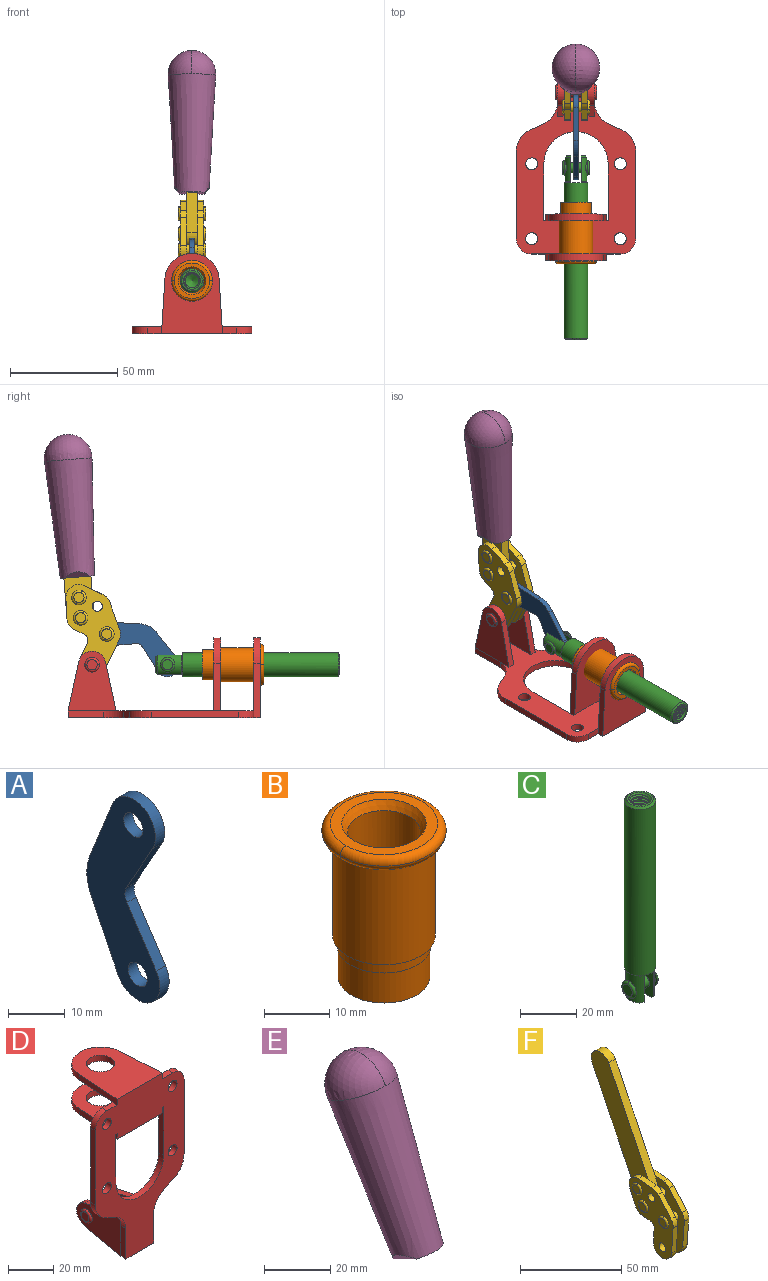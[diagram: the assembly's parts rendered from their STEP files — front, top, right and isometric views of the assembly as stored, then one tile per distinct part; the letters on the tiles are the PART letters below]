
ASSEMBLY  parts=6 mates=6
PART A: 12 faces, bbox 2.3x18.2x42.8 mm
  f0: cylinder r=2.4mm len=4.8mm, axis (1,0,0), area 34.9mm2, adj f4,f11
  f1: cylinder r=10.41mm len=8.47mm, axis (1,0,0), area 20.2mm2, adj f4,f9,f10,f11
  f2: cylinder r=3.05mm len=3.16mm, axis (1,0,0), area 7.7mm2, adj f4,f6,f7,f11
  f3: cylinder r=2.4mm len=4.8mm, axis (1,0,0), area 34.9mm2, adj f4,f11
  f4: plane 42.81x18.23mm, normal (-1,0,0), area 414.1mm2, adj f0,f1,f2,f3,f5,f6,f7,f8
  f5: cylinder r=5.54mm len=10.67mm, axis (1,0,0), area 41.8mm2, adj f4,f6,f10,f11
  f6: plane 11.66x6.53mm, normal (0,-0.87,-0.49), area 30.9mm2, adj f2,f4,f5,f11
  f7: plane 11.17x7.33mm, normal (0,-0.84,0.55), area 30.9mm2, adj f2,f4,f8,f11
  f8: cylinder r=5.54mm len=10.51mm, axis (1,0,0), area 41.8mm2, adj f4,f7,f9,f11
  f9: plane 13.67x6.67mm, normal (0,0.9,-0.44), area 35.1mm2, adj f1,f4,f8,f11
  f10: plane 14.1x5.7mm, normal (0,0.93,0.37), area 35.1mm2, adj f1,f4,f5,f11
  f11: plane 42.81x18.23mm, normal (1,0,0), area 414.1mm2, adj f0,f1,f2,f3,f5,f6,f7,f8
PART B: 15 faces, bbox 20.6x20.6x28.7 mm
  f0: torus R=8.26mm, axis (0,0,1), area 56.8mm2, adj f1,f10,f12
  f1: torus R=8.26mm, axis (0,0,1), area 56.8mm2, adj f0,f6,f13
  f2: cylinder r=5.59mm len=25.91mm, axis (0,0,1), area 909.6mm2, adj f3,f4
  f3: cone r=6.86mm half-angle=45deg, axis (0,0,-1), area 70.2mm2, adj f2,f14
  f4: cone r=6.47mm half-angle=30deg, axis (0,0,1), area 66.7mm2, adj f2,f13
  f5: cylinder r=7.04mm len=14.07mm, axis (0,0,1), area 252.6mm2, adj f11,f14
  f6: torus R=8.26mm, axis (0,0,1), area 56.8mm2, adj f1,f12,f13
  f7: cylinder r=7.16mm len=14.33mm, axis (0,0,1), area 91.5mm2, adj f9,f11
  f8: cylinder r=7.86mm len=18.42mm, axis (0,0,1), area 909.6mm2, adj f9,f10
  f9: plane 15.72x15.72mm, normal (0,0,-1), area 33mm2, adj f7,f8
  f10: plane 16.51x16.51mm, normal (0,0,-1), area 19.9mm2, adj f0,f8,f12
  f11: plane 14.33x14.33mm, normal (0,0,-1), area 5.7mm2, adj f5,f7
  f12: torus R=8.26mm, axis (0,0,1), area 56.8mm2, adj f0,f6,f10
  f13: plane 16.51x16.51mm, normal (0,0,1), area 82.7mm2, adj f1,f4,f6
  f14: plane 14.07x14.07mm, normal (0,0,-1), area 7.8mm2, adj f3,f5
PART C: 48 faces, bbox 12.6x11.1x86.1 mm
  f0: torus R=2.41mm, axis (-1,0,0), area 15mm2, adj f30,f32,f34
  f1: torus R=2.41mm, axis (-1,0,0), area 15mm2, adj f29,f31,f33
  f2: cylinder r=5.54mm len=72.39mm, axis (0,0,1), area 2518.5mm2, adj f3,f4,f42,f43
  f3: cone r=5.54mm half-angle=45deg, axis (0,0,1), area 7.6mm2, adj f2,f5,f41
  f4: cone r=5.54mm half-angle=45deg, axis (0,0,-1), area 34.9mm2, adj f2,f39
  f5: cylinder r=5.08mm len=11.48mm, axis (0,0,1), area 108.3mm2, adj f3,f7,f8,f41
  f6: cylinder r=2.41mm len=4.83mm, axis (-1,0,0), area 71.2mm2, adj f40,f41
  f7: cylinder r=2.41mm len=4.83mm, axis (-1,0,0), area 7.6mm2, adj f5,f34
  f8: cone r=5.08mm half-angle=45deg, axis (0,0,1), area 10.6mm2, adj f5,f37,f41
  f9: cone r=3.98mm half-angle=45deg, axis (0,0,1), area 17.6mm2, adj f27,f39,f45,f46,f47
  f10: cylinder r=2.41mm len=4.83mm, axis (-1,0,0), area 7.6mm2, adj f33,f38
  f11: cylinder r=3.2mm len=6.4mm, axis (0,0,1), area 78.4mm2, adj f12,f28,f44,f45,f47
  f12: cylinder r=3.2mm len=6.4mm, axis (0,0,1), area 10.5mm2, adj f11,f13,f45,f47
  f13: cylinder r=3.2mm len=6.4mm, axis (0,0,1), area 10.5mm2, adj f12,f14,f45,f47
  f14: cylinder r=3.2mm len=6.4mm, axis (0,0,1), area 10.5mm2, adj f13,f15,f45,f47
  f15: cylinder r=3.2mm len=6.4mm, axis (0,0,1), area 10.5mm2, adj f14,f16,f45,f47
  f16: cylinder r=3.2mm len=6.4mm, axis (0,0,1), area 10.5mm2, adj f15,f17,f45,f47
  f17: cylinder r=3.2mm len=6.4mm, axis (0,0,1), area 10.5mm2, adj f16,f18,f45,f47
  f18: cylinder r=3.2mm len=6.4mm, axis (0,0,1), area 10.5mm2, adj f17,f19,f45,f47
  f19: cylinder r=3.2mm len=6.4mm, axis (0,0,1), area 10.5mm2, adj f18,f20,f45,f47
  f20: cylinder r=3.2mm len=6.4mm, axis (0,0,1), area 10.5mm2, adj f19,f21,f45,f47
  f21: cylinder r=3.2mm len=6.4mm, axis (0,0,1), area 10.5mm2, adj f20,f22,f45,f47
  f22: cylinder r=3.2mm len=6.4mm, axis (0,0,1), area 10.5mm2, adj f21,f23,f45,f47
  f23: cylinder r=3.2mm len=6.4mm, axis (0,0,1), area 10.5mm2, adj f22,f24,f45,f47
  f24: cylinder r=3.2mm len=6.4mm, axis (0,0,1), area 10.5mm2, adj f23,f25,f45,f47
  f25: cylinder r=3.2mm len=6.4mm, axis (0,0,1), area 10.5mm2, adj f24,f26,f45,f47
  f26: cylinder r=3.2mm len=6.4mm, axis (0,0,1), area 10.5mm2, adj f25,f27,f45,f47
  f27: cylinder r=3.2mm len=6.4mm, axis (0,0,1), area 7.4mm2, adj f9,f26,f45,f47
  f28: cone r=3.2mm half-angle=60deg, axis (0,0,1), area 37.2mm2, adj f11
  f29: plane 4.83x4.83mm, normal (-1,0,0), area 18.3mm2, adj f1,f31
  f30: plane 4.83x4.83mm, normal (1,0,0), area 18.3mm2, adj f0,f32
  f31: torus R=2.41mm, axis (-1,0,0), area 15mm2, adj f1,f29,f33
  f32: torus R=2.41mm, axis (-1,0,0), area 15mm2, adj f0,f30,f34
  f33: plane 6.83x6.83mm, normal (1,0,0), area 18.3mm2, adj f1,f10,f31
  f34: plane 6.83x6.83mm, normal (-1,0,0), area 18.3mm2, adj f0,f7,f32
  f35: cone r=5.08mm half-angle=45deg, axis (0,0,1), area 10.6mm2, adj f36,f38,f40
  f36: plane 7.25x1.97mm, normal (0,0,-1), area 10mm2, adj f35,f40
  f37: plane 7.25x1.97mm, normal (0,0,-1), area 10mm2, adj f8,f41
  f38: cylinder r=5.08mm len=11.48mm, axis (0,0,1), area 108.3mm2, adj f10,f35,f40,f42
  f39: plane 9.55x9.55mm, normal (0,0,1), area 22mm2, adj f4,f9
  f40: plane 12.76x10.09mm, normal (1,0,0), area 95.7mm2, adj f6,f35,f36,f38,f42,f43
  f41: plane 12.76x10.09mm, normal (-1,0,0), area 95.7mm2, adj f3,f5,f6,f8,f37,f43
  f42: cone r=5.54mm half-angle=45deg, axis (0,0,1), area 7.6mm2, adj f2,f38,f40
  f43: plane 11.07x4.7mm, normal (0,0,-1), area 50.4mm2, adj f2,f40,f41
  f44: plane 0.89x0.62mm, normal (-1,0,0), area 0.3mm2, adj f11,f45,f46,f47
  f45: bspline ~24.8x7.63mm, area 266.6mm2, adj f9,f11,f12,f13,f14,f15,f16,f17
  f46: bspline ~24.87x7.63mm, area 73.6mm2, adj f9,f44,f45,f47
  f47: bspline ~24.98x7.63mm, area 272.5mm2, adj f9,f11,f12,f13,f14,f15,f16,f17
PART D: 55 faces, bbox 55.7x37.4x89.8 mm
  f0: torus R=2.41mm, axis (-1,0,0), area 15mm2, adj f11,f15,f25
  f1: torus R=2.41mm, axis (-1,0,0), area 15mm2, adj f10,f12,f22
  f2: cylinder r=2.78mm len=5.56mm, axis (0,-1,0), area 54.2mm2, adj f30,f54
  f3: cylinder r=14.99mm len=29.97mm, axis (0,-1,0), area 145.9mm2, adj f30,f49,f53,f54
  f4: cylinder r=2.78mm len=5.56mm, axis (0,-1,0), area 54.2mm2, adj f30,f54
  f5: cylinder r=2.78mm len=5.56mm, axis (0,-1,0), area 54.2mm2, adj f30,f54
  f6: cylinder r=2.78mm len=5.56mm, axis (0,-1,0), area 54.2mm2, adj f30,f54
  f7: cylinder r=6.35mm len=12.7mm, axis (0,0,1), area 123.6mm2, adj f27,f51
  f8: cylinder r=6.35mm len=12.7mm, axis (0,0,-1), area 124.7mm2, adj f21,f35
  f9: cylinder r=2.41mm len=11.18mm, axis (-1,0,0), area 169.4mm2, adj f16,f19
  f10: plane 4.83x4.83mm, normal (1,0,0), area 18.3mm2, adj f1,f12
  f11: plane 4.83x4.83mm, normal (-1,0,0), area 18.3mm2, adj f0,f15
  f12: torus R=2.41mm, axis (-1,0,0), area 15mm2, adj f1,f10,f22
  f13: cylinder r=6.35mm len=12.41mm, axis (1,0,0), area 53.4mm2, adj f18,f19,f22,f23
  f14: cylinder r=6.35mm len=12.41mm, axis (-1,0,0), area 53.4mm2, adj f16,f17,f24,f25
  f15: torus R=2.41mm, axis (-1,0,0), area 15mm2, adj f0,f11,f25
  f16: plane 27.86x22.35mm, normal (1,0,0), area 425.4mm2, adj f9,f14,f17,f24,f30
  f17: plane 22.86x4.97mm, normal (0,0.21,0.98), area 72.5mm2, adj f14,f16,f25,f30
  f18: plane 22.86x4.97mm, normal (0,0.21,0.98), area 72.5mm2, adj f13,f19,f22,f30
  f19: plane 27.86x22.35mm, normal (-1,0,0), area 425.4mm2, adj f9,f13,f18,f23,f30
  f20: cylinder r=12.7mm len=25.35mm, axis (0,0,-1), area 119.8mm2, adj f21,f34,f35,f36
  f21: plane 34.21x28.07mm, normal (0,0,-1), area 702.4mm2, adj f8,f20,f30,f34,f36
  f22: plane 27.96x22.45mm, normal (1,0,0), area 407.2mm2, adj f1,f12,f13,f18,f23,f30,f42,f43
  f23: plane 22.86x4.97mm, normal (0,0.21,-0.98), area 72.5mm2, adj f13,f19,f22,f44
  f24: plane 22.86x4.97mm, normal (0,0.21,-0.98), area 72.5mm2, adj f14,f16,f25,f44
  f25: plane 27.86x22.35mm, normal (-1,0,0), area 407.1mm2, adj f0,f14,f15,f17,f24,f30,f45,f46
  f26: plane 3.1x0.95mm, normal (0,0,-1), area 2.7mm2, adj f30,f49,f50,f54
  f27: plane 34.21x28.07mm, normal (0,0,1), area 702.4mm2, adj f7,f28,f30,f50,f52
  f28: cylinder r=12.7mm len=25.35mm, axis (0,0,1), area 118.8mm2, adj f27,f50,f51,f52
  f29: plane 3.1x0.95mm, normal (0,0,-1), area 2.7mm2, adj f30,f52,f53,f54
  f30: plane 86.54x55.63mm, normal (0,1,0), area 2362.9mm2, adj f2,f3,f4,f5,f6,f16,f17,f18
  f31: plane 40.56x3.1mm, normal (-1,0,0), area 125.7mm2, adj f30,f32,f48,f54
  f32: cylinder r=7.11mm len=7.11mm, axis (0,-1,0), area 34.6mm2, adj f30,f31,f33,f54
  f33: plane 6.67x3.1mm, normal (0,0,1), area 20.4mm2, adj f30,f32,f34,f54
  f34: plane 25.39x3.13mm, normal (-1,0.06,0), area 79.5mm2, adj f20,f21,f33,f35,f54
  f35: plane 37.31x28.45mm, normal (0,0,1), area 789.9mm2, adj f8,f20,f34,f36,f54
  f36: plane 25.39x3.13mm, normal (1,0.06,0), area 79.5mm2, adj f20,f21,f35,f37,f54
  f37: plane 6.67x3.1mm, normal (0,0,1), area 20.4mm2, adj f30,f36,f38,f54
  f38: cylinder r=7.11mm len=7.11mm, axis (0,-1,0), area 34.6mm2, adj f30,f37,f39,f54
  f39: plane 40.56x3.1mm, normal (1,0,0), area 125.7mm2, adj f30,f38,f40,f54
  f40: cylinder r=11.18mm len=10.16mm, axis (0,-1,0), area 39.5mm2, adj f30,f39,f41,f54
  f41: plane 6.09x3.1mm, normal (0.42,0,-0.91), area 20.8mm2, adj f30,f40,f42,f54
  f42: cylinder r=11.18mm len=9.41mm, axis (0,-1,0), area 37.2mm2, adj f22,f30,f41,f43,f54
  f43: plane 16.5x3.1mm, normal (1,0,0), area 51.1mm2, adj f22,f42,f44,f54
  f44: plane 17.37x3.1mm, normal (0,0,-1), area 53.8mm2, adj f23,f24,f30,f43,f45,f54
  f45: plane 16.5x3.1mm, normal (-1,0,0), area 51.1mm2, adj f25,f44,f46,f54
  f46: cylinder r=11.18mm len=9.41mm, axis (0,-1,0), area 37.2mm2, adj f25,f30,f45,f47,f54
  f47: plane 6.09x3.1mm, normal (-0.42,0,-0.91), area 20.8mm2, adj f30,f46,f48,f54
  f48: cylinder r=11.18mm len=10.16mm, axis (0,-1,0), area 39.5mm2, adj f30,f31,f47,f54
  f49: plane 26.54x3.1mm, normal (-1,0,0), area 82.3mm2, adj f3,f26,f30,f54
  f50: plane 25.39x3.1mm, normal (1,0.06,0), area 78.8mm2, adj f26,f27,f28,f51,f54
  f51: plane 37.31x28.45mm, normal (0,0,-1), area 789.9mm2, adj f7,f28,f50,f52,f54
  f52: plane 25.39x3.1mm, normal (-1,0.06,0), area 78.8mm2, adj f27,f28,f29,f51,f54
  f53: plane 26.54x3.1mm, normal (1,0,0), area 82.3mm2, adj f3,f29,f30,f54
  f54: plane 89.66x55.63mm, normal (0,-1,0), area 2678.5mm2, adj f2,f3,f4,f5,f6,f26,f29,f31
PART E: 11 faces, bbox 22.3x42.6x64.5 mm
  f0: sphere r=11.13mm, area 411.4mm2, adj f1,f8
  f1: cone r=11.11mm half-angle=3.3deg, axis (0,0.44,0.9), area 3251.8mm2, adj f0,f7,f8,f9,f10
  f2: cylinder r=6.16mm len=11.7mm, axis (1,0,0), area 89.5mm2, adj f3,f4,f5,f6
  f3: plane 60.23x36.75mm, normal (-1,0,0), area 763.6mm2, adj f2,f4,f6,f10
  f4: plane 51.37x25.05mm, normal (0,0.9,-0.44), area 264.2mm2, adj f2,f3,f5,f10
  f5: plane 60.23x36.75mm, normal (1,0,0), area 763.6mm2, adj f2,f4,f6,f10
  f6: plane 51.37x25.05mm, normal (0,-0.9,0.44), area 264.2mm2, adj f2,f3,f5,f10
  f7: plane 9.95x5.95mm, normal (0.71,-0.31,-0.64), area 25.8mm2, adj f1,f10
  f8: sphere r=11.13mm, area 411.4mm2, adj f0,f1
  f9: plane 9.95x5.95mm, normal (-0.71,-0.31,-0.64), area 25.8mm2, adj f1,f10
  f10: plane 14.27x11.38mm, normal (0,-0.44,-0.9), area 106.7mm2, adj f1,f3,f4,f5,f6,f7,f9
PART F: 59 faces, bbox 12.9x60.2x99.6 mm
  f0: torus R=2.39mm, axis (-1,0,0), area 14.9mm2, adj f20,f43,f51
  f1: torus R=2.39mm, axis (-1,0,0), area 14.9mm2, adj f19,f42,f51
  f2: torus R=2.39mm, axis (-1,0,0), area 14.9mm2, adj f18,f35,f51
  f3: torus R=2.39mm, axis (-1,0,0), area 14.9mm2, adj f14,f17,f23
  f4: torus R=2.39mm, axis (-1,0,0), area 14.9mm2, adj f13,f16,f23
  f5: torus R=2.39mm, axis (-1,0,0), area 14.9mm2, adj f12,f15,f23
  f6: cylinder r=2.39mm len=4.78mm, axis (1,0,0), area 46.5mm2, adj f48,f50,f51
  f7: cylinder r=2.39mm len=4.78mm, axis (1,0,0), area 46.5mm2, adj f50,f51
  f8: cylinder r=6.35mm len=12.68mm, axis (1,0,0), area 61.8mm2, adj f38,f39,f50,f51
  f9: cylinder r=2.39mm len=4.78mm, axis (-1,0,0), area 70.5mm2, adj f46,f50
  f10: cylinder r=2.39mm len=4.78mm, axis (-1,0,0), area 46.5mm2, adj f23,f45,f46
  f11: cylinder r=2.39mm len=4.78mm, axis (-1,0,0), area 46.5mm2, adj f23,f46
  f12: plane 4.78x4.78mm, normal (1,0,0), area 17.9mm2, adj f5,f15
  f13: plane 4.78x4.78mm, normal (1,0,0), area 17.9mm2, adj f4,f16
  f14: plane 4.78x4.78mm, normal (1,0,0), area 17.9mm2, adj f3,f17
  f15: torus R=2.39mm, axis (-1,0,0), area 14.9mm2, adj f5,f12,f23
  f16: torus R=2.39mm, axis (-1,0,0), area 14.9mm2, adj f4,f13,f23
  f17: torus R=2.39mm, axis (-1,0,0), area 14.9mm2, adj f3,f14,f23
  f18: plane 4.78x4.78mm, normal (-1,0,0), area 17.9mm2, adj f2,f35
  f19: plane 4.78x4.78mm, normal (-1,0,0), area 17.9mm2, adj f1,f42
  f20: plane 4.78x4.78mm, normal (-1,0,0), area 17.9mm2, adj f0,f43
  f21: plane 2.26x0.2mm, normal (1,0,0), area 0.2mm2, adj f31,f44
  f22: plane 2.26x0.2mm, normal (-1,0,0), area 0.2mm2, adj f41,f44
  f23: plane 39.37x30.77mm, normal (1,0,0), area 565.5mm2, adj f3,f4,f5,f10,f11,f15,f16,f17
  f24: cylinder r=6.1mm len=4.15mm, axis (-1,0,0), area 14.7mm2, adj f23,f25,f32,f46
  f25: plane 10.25x9.01mm, normal (0,-0.75,0.66), area 42.3mm2, adj f23,f24,f26,f46
  f26: cylinder r=6.35mm len=4.64mm, axis (-1,0,0), area 15.6mm2, adj f23,f25,f27,f46
  f27: plane 15.84x3.1mm, normal (0,-1,-0.07), area 49.2mm2, adj f23,f26,f28,f46
  f28: cylinder r=6.35mm len=12.68mm, axis (-1,0,0), area 61.8mm2, adj f23,f27,f29,f46
  f29: plane 8.11x3.1mm, normal (0,1,0.07), area 25.2mm2, adj f23,f28,f30,f46
  f30: cylinder r=3.05mm len=3.25mm, axis (-1,0,0), area 14.8mm2, adj f23,f29,f31,f46
  f31: plane 5.99x3.1mm, normal (0,0.07,-1), area 18.6mm2, adj f21,f23,f30,f44,f46
  f32: plane 9.5x3.1mm, normal (0,-0.07,1), area 29.5mm2, adj f23,f24,f33,f46,f47
  f33: cylinder r=6.1mm len=8.63mm, axis (-1,0,0), area 39.1mm2, adj f23,f32,f34,f47
  f34: plane 8.65x3.96mm, normal (0,0.91,-0.42), area 29.5mm2, adj f23,f33,f44,f47
  f35: torus R=2.39mm, axis (-1,0,0), area 14.9mm2, adj f2,f18,f51
  f36: plane 10.25x9.01mm, normal (0,-0.75,0.66), area 42.3mm2, adj f37,f49,f50,f51
  f37: cylinder r=6.35mm len=4.64mm, axis (1,0,0), area 15.6mm2, adj f36,f38,f50,f51
  f38: plane 15.84x3.1mm, normal (0,-1,-0.07), area 49.2mm2, adj f8,f37,f50,f51
  f39: plane 8.11x3.1mm, normal (0,1,0.07), area 25.2mm2, adj f8,f40,f50,f51
  f40: cylinder r=3.05mm len=3.25mm, axis (1,0,0), area 14.8mm2, adj f39,f41,f50,f51
  f41: plane 5.99x3.1mm, normal (0,0.07,-1), area 18.6mm2, adj f22,f40,f44,f50,f51
  f42: torus R=2.39mm, axis (-1,0,0), area 14.9mm2, adj f1,f19,f51
  f43: torus R=2.39mm, axis (-1,0,0), area 14.9mm2, adj f0,f20,f51
  f44: cylinder r=6.35mm len=12.12mm, axis (-1,0,0), area 128.9mm2, adj f21,f22,f23,f31,f34,f41,f46,f47
  f45: plane 2.65x1.35mm, normal (1,0,0), area 1mm2, adj f10,f55
  f46: plane 39.08x20.42mm, normal (-1,0,0), area 412.5mm2, adj f9,f10,f11,f24,f25,f26,f27,f28
  f47: plane 77.62x39.82mm, normal (1,0,0), area 850mm2, adj f32,f33,f34,f44,f53,f54,f55
  f48: plane 2.65x1.35mm, normal (-1,0,0), area 1mm2, adj f6,f55
  f49: cylinder r=6.1mm len=4.15mm, axis (1,0,0), area 14.7mm2, adj f36,f50,f51,f56
  f50: plane 39.08x20.42mm, normal (1,0,0), area 412.5mm2, adj f6,f7,f8,f9,f36,f37,f38,f39
  f51: plane 39.37x30.77mm, normal (-1,0,0), area 565.5mm2, adj f0,f1,f2,f6,f7,f8,f35,f36
  f52: plane 8.65x3.96mm, normal (0,0.91,-0.42), area 29.5mm2, adj f44,f51,f57,f58
  f53: plane 68.49x33.4mm, normal (0,0.9,-0.44), area 358.1mm2, adj f44,f47,f54,f58
  f54: cylinder r=6.35mm len=12.06mm, axis (1,0,0), area 93.7mm2, adj f47,f53,f55,f58
  f55: plane 68.49x33.4mm, normal (0,-0.9,0.44), area 358.1mm2, adj f44,f45,f46,f47,f48,f50,f54,f58
  f56: plane 9.5x3.1mm, normal (0,-0.07,1), area 29.5mm2, adj f49,f50,f51,f57,f58
  f57: cylinder r=6.1mm len=8.63mm, axis (1,0,0), area 39.1mm2, adj f51,f52,f56,f58
  f58: plane 77.62x39.82mm, normal (-1,0,0), area 850mm2, adj f44,f52,f53,f54,f55,f56,f57
PLACE A rot(axis=(1,0,0),118.8deg) t=(0,31.47,10.51)mm
PLACE B rot(axis=(1,0,0),90deg) t=(0,10.16,0)mm
PLACE C rot(axis=(1,0,0),90deg) t=(0,21.53,0)mm
PLACE D rot(axis=(1,0,0),90deg) t=(0,9.14,0)mm fixed
PLACE E rot(axis=(1,0,0),21.5deg) t=(-0.04,6.56,45.43)mm
PLACE F rot(axis=(1,0,0),21.5deg) t=(0,6.56,45.43)mm
MATE revolute F.f7 <-> D.f0  axis (-1,0,0) through (0,41.23,24.61)mm
MATE revolute A.f3 <-> F.f4  axis (1,0,0) through (0,34.39,38.94)mm
MATE fastened E.f2 <-> F.f54  axis (1,0,0) through (-2.35,52.53,122.46)mm
MATE fastened C.f2 <-> B.f2  axis (0,-1,0) through (0,-37.25,24.61)mm
MATE fastened B.f2 <-> D.f7  axis (0,-1,0) through (0,-37.25,24.61)mm
MATE revolute A.f5 <-> C.f6  axis (1,0,0) through (0,6.05,24.61)mm
